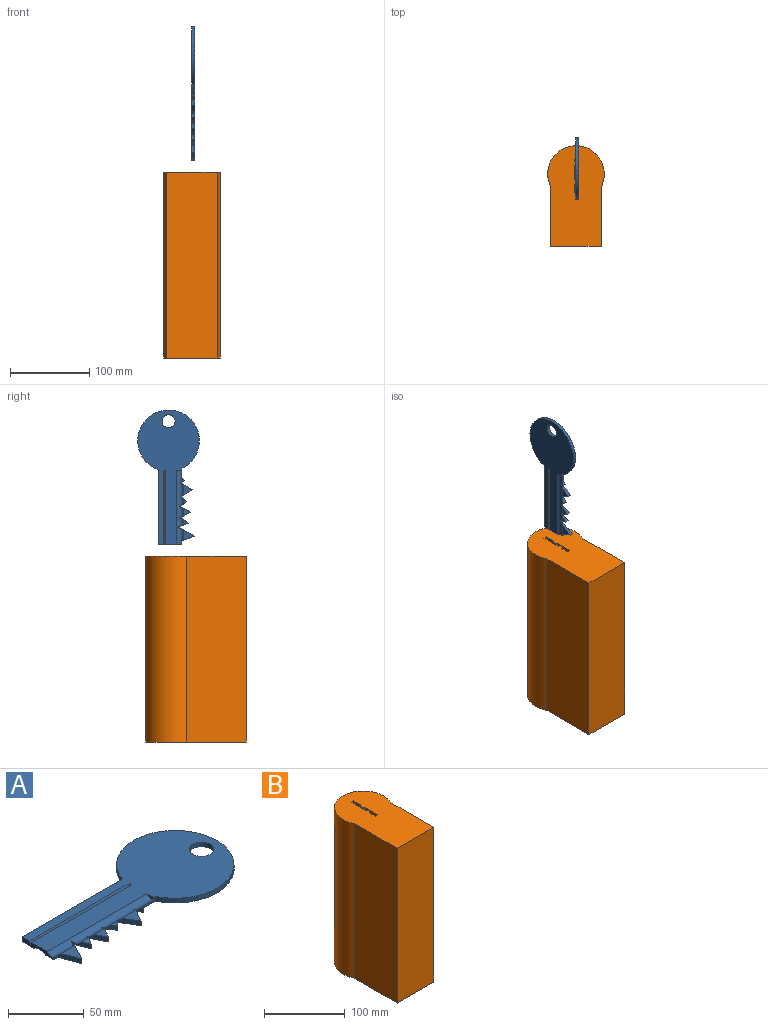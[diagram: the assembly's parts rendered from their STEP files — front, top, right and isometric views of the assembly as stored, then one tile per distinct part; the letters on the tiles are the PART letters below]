
ASSEMBLY  parts=2 mates=1
PART A: 33 faces, bbox 169.3x77.8x4 mm
  f0: plane 29.75x4mm, normal (-1,0,0), area 84.5mm2, adj f7,f8,f16,f17,f26,f28,f29,f31
  f1: plane 14.05x12.88mm, normal (0,0,1), area 90.5mm2, adj f18,f19,f31
  f2: plane 6.68x6.53mm, normal (0,0,1), area 21.8mm2, adj f20,f21,f31
  f3: plane 9.5x9.27mm, normal (0,0,1), area 44mm2, adj f22,f23,f31
  f4: plane 6.78x3.8mm, normal (0,0,1), area 12.9mm2, adj f9,f25,f31
  f5: plane 13.01x11.49mm, normal (0,0,1), area 74.8mm2, adj f10,f11,f31
  f6: plane 2.08x1.74mm, normal (0,0,1), area 1.8mm2, adj f12,f13,f31
  f7: plane 169.33x77.77mm, normal (0,0,1), area 6504.5mm2, adj f0,f14,f15,f16,f24,f28,f29,f30
  f8: plane 169.33x77.77mm, normal (0,0,-1), area 6570.3mm2, adj f0,f9,f10,f11,f12,f13,f14,f15
  f9: plane 6.5x6.33mm, normal (0.72,-0.7,0), area 29.4mm2, adj f4,f8,f10,f25,f31
  f10: plane 14.19x8.21mm, normal (-0.87,-0.5,0), area 58.2mm2, adj f5,f8,f9,f11,f31
  f11: plane 15.73x8.72mm, normal (0.87,-0.48,0), area 60.2mm2, adj f5,f8,f10,f12,f31
  f12: plane 5.98x3.81mm, normal (-0.88,-0.48,0), area 17.7mm2, adj f6,f8,f11,f13,f31
  f13: plane 3.81x3.76mm, normal (0.84,-0.54,0), area 14.3mm2, adj f6,f8,f12,f14,f31
  f14: plane 12.39x3.81mm, normal (0,-1,0), area 27.4mm2, adj f7,f8,f13,f15,f31,f32
  f15: cylinder r=38.88mm len=77.77mm, axis (0,0,-1), area 814.4mm2, adj f7,f8,f14,f16
  f16: plane 93.8x3.81mm, normal (0,1,0), area 357.4mm2, adj f0,f7,f8,f15
  f17: plane 3.92x1.91mm, normal (0,-1,0), area 7.5mm2, adj f0,f8,f18,f31
  f18: plane 16.07x6.17mm, normal (-0.93,-0.36,0), area 63.1mm2, adj f1,f8,f17,f19,f31
  f19: plane 20.86x11.11mm, normal (0.88,-0.47,0), area 75.7mm2, adj f1,f8,f18,f20,f31
  f20: plane 13.34x5.3mm, normal (-0.93,-0.37,0), area 41.1mm2, adj f2,f8,f19,f21,f31
  f21: plane 10.94x6.84mm, normal (0.85,-0.53,0), area 40.1mm2, adj f2,f8,f20,f22,f31
  f22: plane 13.68x7.01mm, normal (-0.89,-0.46,0), area 49.9mm2, adj f3,f8,f21,f23,f31
  f23: plane 13.68x7.01mm, normal (0.89,-0.46,0), area 49.9mm2, adj f3,f8,f22,f25,f31
  f24: cylinder r=8.18mm len=16.36mm, axis (0,0,-1), area 195.8mm2, adj f7,f8
  f25: plane 8.21x6.67mm, normal (-0.78,-0.63,0), area 30.4mm2, adj f4,f8,f9,f23,f31
  f26: extruded ~93.35x11.41mm, area 1146.2mm2, adj f0,f8,f27
  f27: plane 11.79x2.36mm, normal (-1,0,0), area 15mm2, adj f8,f26
  f28: plane 93.35x2.02mm, normal (0,-0.87,0.5), area 217.3mm2, adj f0,f7,f29,f30
  f29: plane 93.35x2.02mm, normal (0,0.87,0.5), area 217.3mm2, adj f0,f7,f28,f30
  f30: plane 2.33x2.02mm, normal (-1,0,0), area 2.3mm2, adj f7,f28,f29
  f31: cylinder r=4.67mm len=93.35mm, axis (-1,0,0), area 799.8mm2, adj f0,f1,f2,f3,f4,f5,f6,f7
  f32: plane 6.12x2.38mm, normal (-1,0,0), area 11.5mm2, adj f7,f14,f31
PART B: 23 faces, bbox 71.4x126.8x234.3 mm
  f0: plane 126.83x71.42mm, normal (0,0,-1), area 7743.6mm2, adj f1,f2,f3,f4,f5,f6,f7,f8
  f1: plane 234.32x10.43mm, normal (1,0,0), area 2443mm2, adj f0,f2,f15,f16
  f2: cylinder r=3.25mm len=234.32mm, axis (0,0,-1), area 2389.2mm2, adj f0,f1,f3,f16
  f3: plane 234.32x17.35mm, normal (1,0,0), area 4066.2mm2, adj f0,f2,f4,f16
  f4: plane 234.32x2.55mm, normal (0.73,-0.68,0), area 815.9mm2, adj f0,f3,f5,f16
  f5: plane 234.32x2.37mm, normal (0.68,0.73,0), area 757.3mm2, adj f0,f4,f6,f16
  f6: plane 234.32x3.27mm, normal (1,0,0), area 766.3mm2, adj f0,f5,f7,f16
  f7: plane 234.32x4.01mm, normal (0,-1,0), area 939.5mm2, adj f0,f6,f8,f16
  f8: plane 234.32x11.95mm, normal (-1,0,0), area 2800.7mm2, adj f0,f7,f9,f16
  f9: cylinder r=5.39mm len=234.32mm, axis (0,0,-1), area 2311.4mm2, adj f0,f8,f10,f16
  f10: plane 234.32x21.8mm, normal (-1,0,0), area 5107.2mm2, adj f0,f9,f15,f16
  f11: plane 234.32x74.63mm, normal (1,0,0), area 17486.6mm2, adj f0,f12,f14,f16
  f12: cylinder r=35.71mm len=234.32mm, axis (0,0,-1), area 34225.4mm2, adj f0,f11,f13,f16
  f13: plane 234.32x74.99mm, normal (-1,0,0), area 17571.1mm2, adj f0,f12,f14,f16
  f14: plane 234.32x63.53mm, normal (0,-1,0), area 14885.2mm2, adj f0,f11,f13,f16
  f15: plane 234.32x4.01mm, normal (0,1,0), area 939.5mm2, adj f0,f1,f10,f16
  f16: plane 126.83x71.42mm, normal (0,0,1), area 7743.6mm2, adj f1,f2,f3,f4,f5,f6,f7,f8
  f17: plane 57.12x53.53mm, normal (0,0,-1), area 3057.4mm2, adj f18,f19,f20,f21
  f18: plane 194.25x53.53mm, normal (0,-1,0), area 10397.5mm2, adj f17,f19,f21,f22
  f19: plane 194.25x57.12mm, normal (-1,0,0), area 11095.4mm2, adj f17,f18,f20,f22
  f20: plane 194.25x53.53mm, normal (0,1,0), area 10397.5mm2, adj f17,f19,f21,f22
  f21: plane 194.25x57.12mm, normal (1,0,0), area 11095.4mm2, adj f17,f18,f20,f22
  f22: plane 57.12x53.53mm, normal (0,0,1), area 3057.4mm2, adj f18,f19,f20,f21
PLACE A rot(axis=(0,-1,0),90deg) t=(231.74,114.5,41.07)mm
PLACE B rot(axis=(0,0,-1),0deg) t=(228.14,77.38,-294.62)mm
MATE slider A.f0 <-> B.f16  axis (0,0,-1) through (229.79,118.47,-44.59)mm
